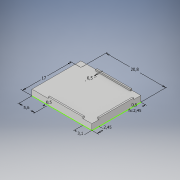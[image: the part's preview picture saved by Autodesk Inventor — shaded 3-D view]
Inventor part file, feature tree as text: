
AUTODESK INVENTOR PART (.ipt)
format: ipt  version: 2019 (Build 230136000, 136)  size: 127,488 bytes
history: native  units: mm
features: extrude x4, sketch x1
ambient origin geometry x8: Origin, YZ Plane, XZ Plane, XY Plane, X Axis, Y Axis, Z Axis, Center Point
bodies: Solid1 (feature_tree)
feature tree (5):
  sketch  "Sketch1"  dims[d0=20.8mm d1=17.0mm d2=0.5mm d3=2.45mm d4=2.45mm d5=3.1mm d6=5.6mm d7=0.5mm d8=0.5mm d9=2.0mm d10=0.0mm d11=2.5mm d12=0.0mm d13=2.5mm d14=0.0mm d15=2.5mm d16=0.0mm]
  extrude  "Extrusion1"  Depth=17.0mm
  extrude  "Extrusion2"  Depth=0.5mm
  extrude  "Extrusion3"  Depth=2.45mm
  extrude  "Extrusion4"  Depth=2.45mm
